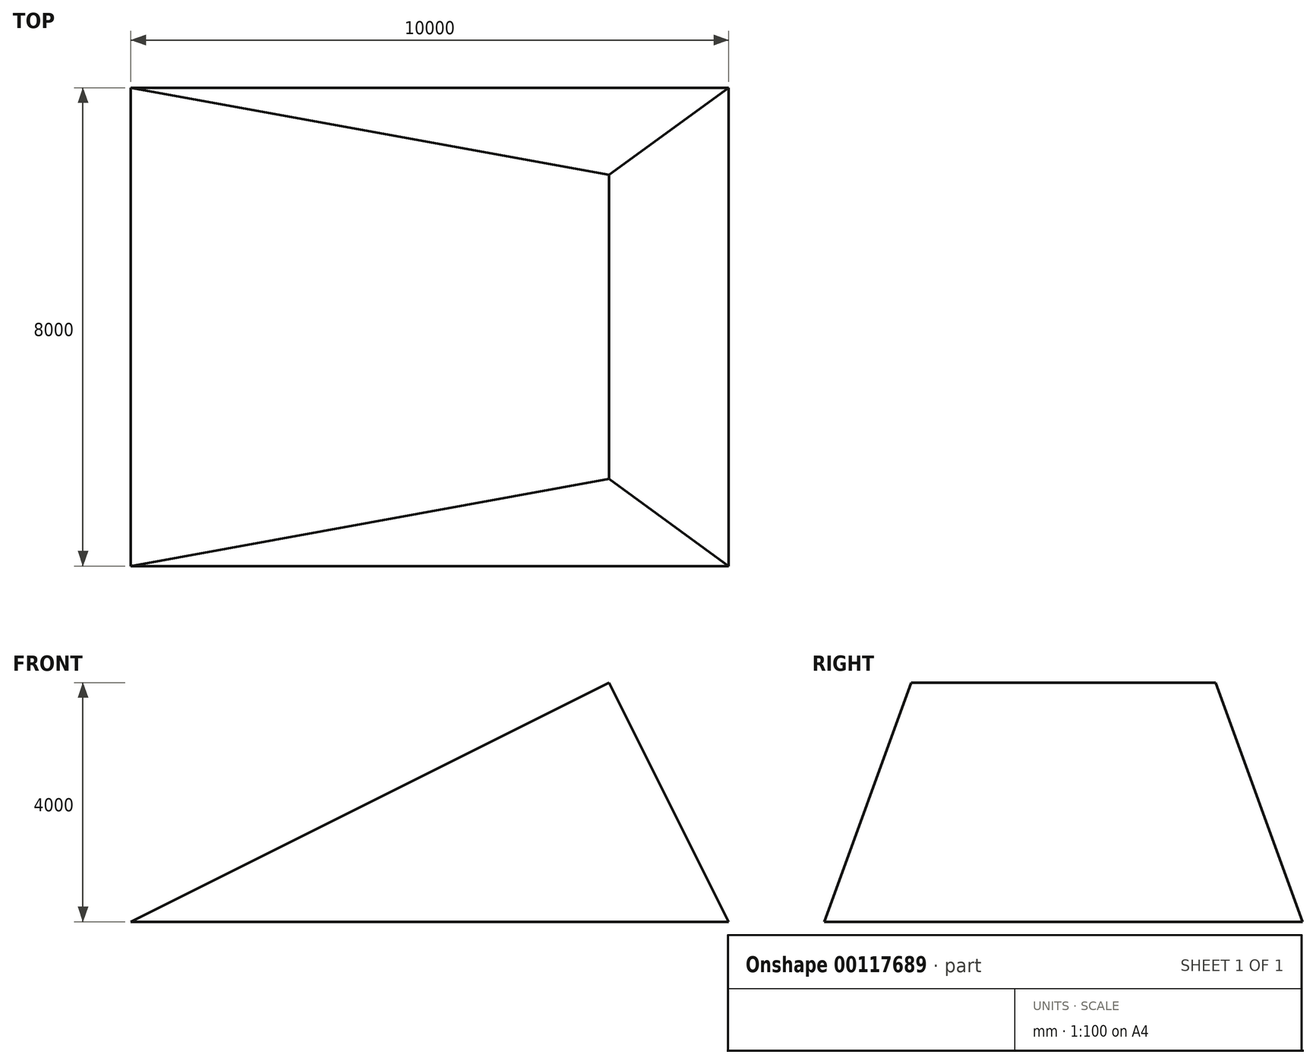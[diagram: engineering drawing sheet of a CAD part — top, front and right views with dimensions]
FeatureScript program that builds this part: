
annotation { "Feature Type Name" : "Feature", "Feature Type Description" : "" }
export const myFeature = defineFeature(function(context is Context, id is Id, definition is map)
    precondition{}
    {
        {
            var Q0;
            Q0=qCreatedBy(makeId("Front.planeOp"),FACE);
            var sketch = newSketch(context, id + "F0", { "sketchPlane" : qUnion([Q0])});
            skLineSegment(sketch, "E0", {"start": v(-5000, 0) * mm, "end": v(5000, 0) * mm});
            skLineSegment(sketch, "E1", {"start": v(5000, 0) * mm, "end": v(3000, 4000) * mm});
            skLineSegment(sketch, "E2", {"start": v(3000, 4000) * mm, "end": v(-5000, 0) * mm});
            skSolve(sketch);
        }
        {
            var Q0;
            Q0=makeQuery(id+"F0.imprint","IMPRINT",FACE,{"disambiguationData":[TD([[makeQuery(id+"F0.imprint","IMPRINT",EDGE,{"derivedFrom":sQuery(id+"F0.wireOp",EDGE,"E0")}),1.0]])]});
            extrude(context, id + "F1", {"entities" : qUnion([Q0]), "depth" : 8000 * mm});
        }
        {
            var Q0;
            Q0=qCreatedBy(makeId("Right.planeOp"),FACE);
            var sketch = newSketch(context, id + "F2", { "sketchPlane" : qUnion([Q0])});
            skLineSegment(sketch, "E3.0.0", {"start": v(0, 4000) * mm, "end": v(0, 0) * mm});
            skLineSegment(sketch, "E3.0.1", {"start": v(0, 0) * mm, "end": v(-8000, 0) * mm, "construction": true});
            skLineSegment(sketch, "E3.0.2", {"start": v(-8000, 0) * mm, "end": v(-8000, 4000) * mm});
            skLineSegment(sketch, "E3.0.3", {"start": v(-8000, 4000) * mm, "end": v(0, 4000) * mm});
            skLineSegment(sketch, "E4", {"start": v(0, 0) * mm, "end": v(-1455.88, 4000) * mm});
            skLineSegment(sketch, "E5", {"start": v(-8000, 0) * mm, "end": v(-6544.12, 4000) * mm});
            skSolve(sketch);
        }
        {
            var Q0;
            {var subQ0=sQuery(id+"F2.wireOp",EDGE,"E3.0.0");Q0=makeQuery(id+"F2.imprint","IMPRINT",FACE,{"disambiguationData":[TD([[makeQuery(id+"F2.imprint","IMPRINT",EDGE,{"derivedFrom":subQ0}),-1.0]])]});}
            var Q1;
            {var subQ0=sQuery(id+"F2.wireOp",EDGE,"E3.0.2");Q1=makeQuery(id+"F2.imprint","IMPRINT",FACE,{"disambiguationData":[TD([[makeQuery(id+"F2.imprint","IMPRINT",EDGE,{"derivedFrom":subQ0}),-1.0]])]});}
            extrude(context, id + "F3", {"entities" : qUnion([Q0, Q1]), "operationType" : NewBodyOperationType.REMOVE, "endBound" : BoundingType.THROUGH_ALL, "oppositeDirection" : true, "depth" : 25 * mm, "hasSecondDirection" : true, "secondDirectionBound" : SecondDirectionBoundingType.THROUGH_ALL, "secondDirectionOppositeDirection" : false, "secondDirectionDepth" : 25 * mm});
        }
    });
